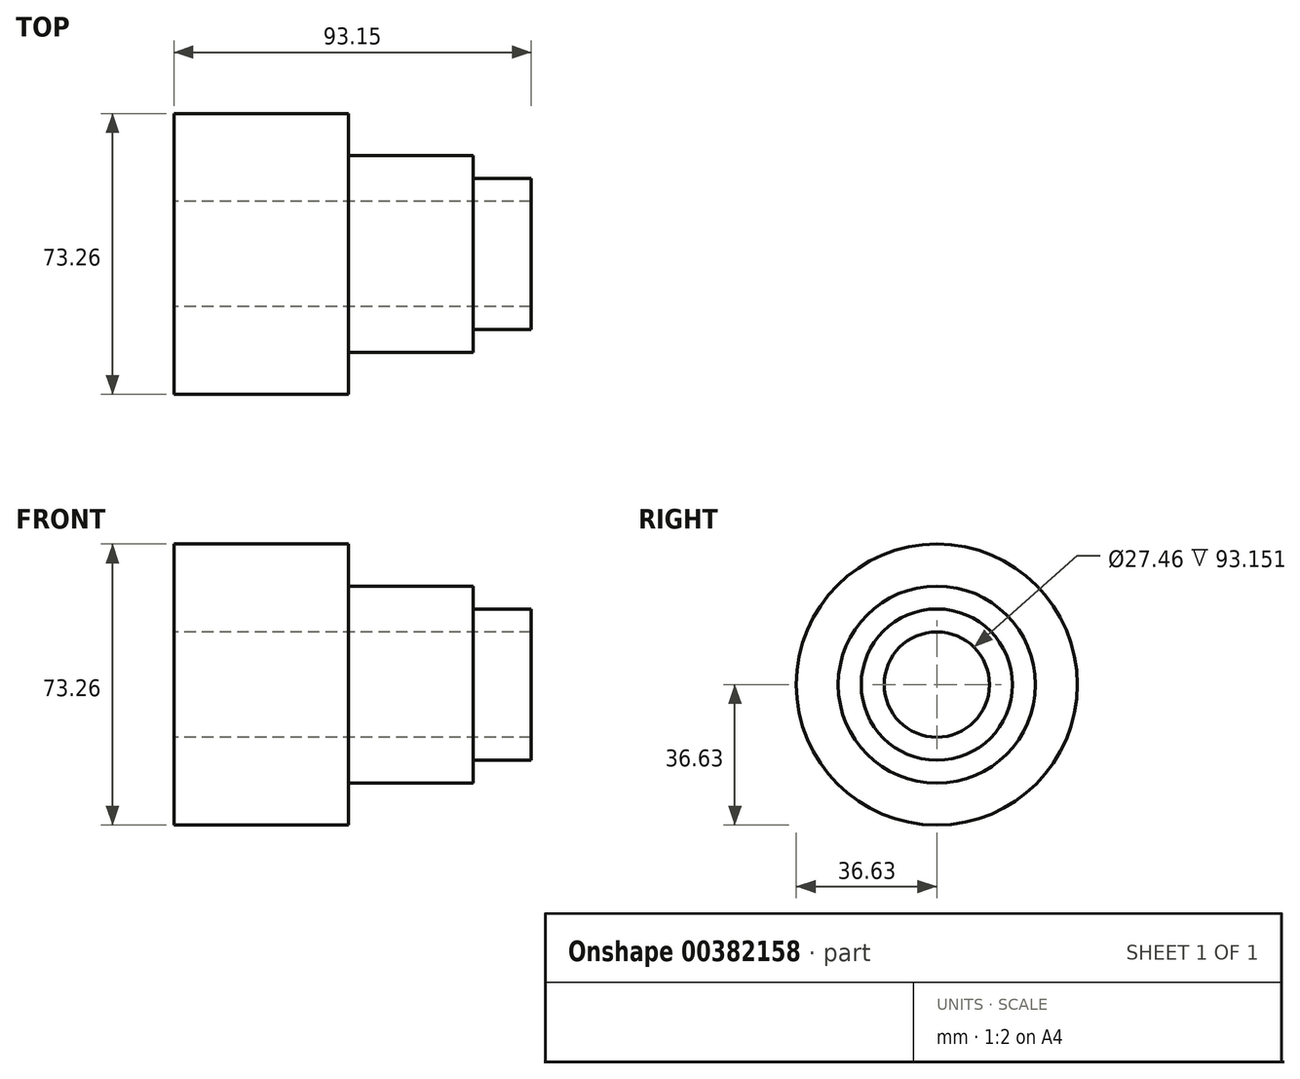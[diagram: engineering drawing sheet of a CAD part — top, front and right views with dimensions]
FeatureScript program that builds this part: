
annotation { "Feature Type Name" : "Feature", "Feature Type Description" : "" }
export const myFeature = defineFeature(function(context is Context, id is Id, definition is map)
    precondition{}
    {
        {
            var Q0;
            Q0=qCreatedBy(makeId("Front.planeOp"),FACE);
            var sketch = newSketch(context, id + "F0", { "sketchPlane" : qUnion([Q0])});
            skLineSegment(sketch, "E0", {"start": v(-48.49, 0) * mm, "end": v(57.63, 0) * mm, "construction": true});
            skLineSegment(sketch, "E1.bottom", {"start": v(-52.4, 36.63) * mm, "end": v(-6.86, 36.63) * mm});
            skLineSegment(sketch, "E1.top", {"start": v(-52.4, 13.73) * mm, "end": v(-6.86, 13.73) * mm});
            skLineSegment(sketch, "E1.left", {"start": v(-52.4, 36.63) * mm, "end": v(-52.4, 13.73) * mm});
            skLineSegment(sketch, "E1.right", {"start": v(-6.86, 36.63) * mm, "end": v(-6.86, 13.73) * mm});
            skLineSegment(sketch, "E2.bottom", {"start": v(-18.3, 25.7) * mm, "end": v(25.67, 25.7) * mm});
            skLineSegment(sketch, "E2.top", {"start": v(-18.3, 13.73) * mm, "end": v(25.67, 13.73) * mm});
            skLineSegment(sketch, "E2.left", {"start": v(-18.3, 25.7) * mm, "end": v(-18.3, 13.73) * mm});
            skLineSegment(sketch, "E2.right", {"start": v(25.67, 25.7) * mm, "end": v(25.67, 13.73) * mm});
            skPoint(sketch, "E3.firstSnap0", {"position": v(25.67, 19.71) * mm});
            skLineSegment(sketch, "E3.bottom", {"start": v(19.42, 19.71) * mm, "end": v(40.76, 19.71) * mm});
            skLineSegment(sketch, "E3.top", {"start": v(19.42, 13.73) * mm, "end": v(40.76, 13.73) * mm});
            skLineSegment(sketch, "E3.left", {"start": v(19.42, 19.71) * mm, "end": v(19.42, 13.73) * mm});
            skLineSegment(sketch, "E3.right", {"start": v(40.76, 19.71) * mm, "end": v(40.76, 13.73) * mm});
            skSolve(sketch);
        }
        {
            var Q0;
            Q0 = qSketchRegion(id + "F0", true);
            var Q1;
            Q1=sQuery(id+"F0.wireOp",EDGE,"E0");
            revolve(context, id + "F1", {"entities" : qUnion([Q0]), "axis" : qUnion([Q1]), "revolveType" : RevolveType.FULL});
        }
    });
